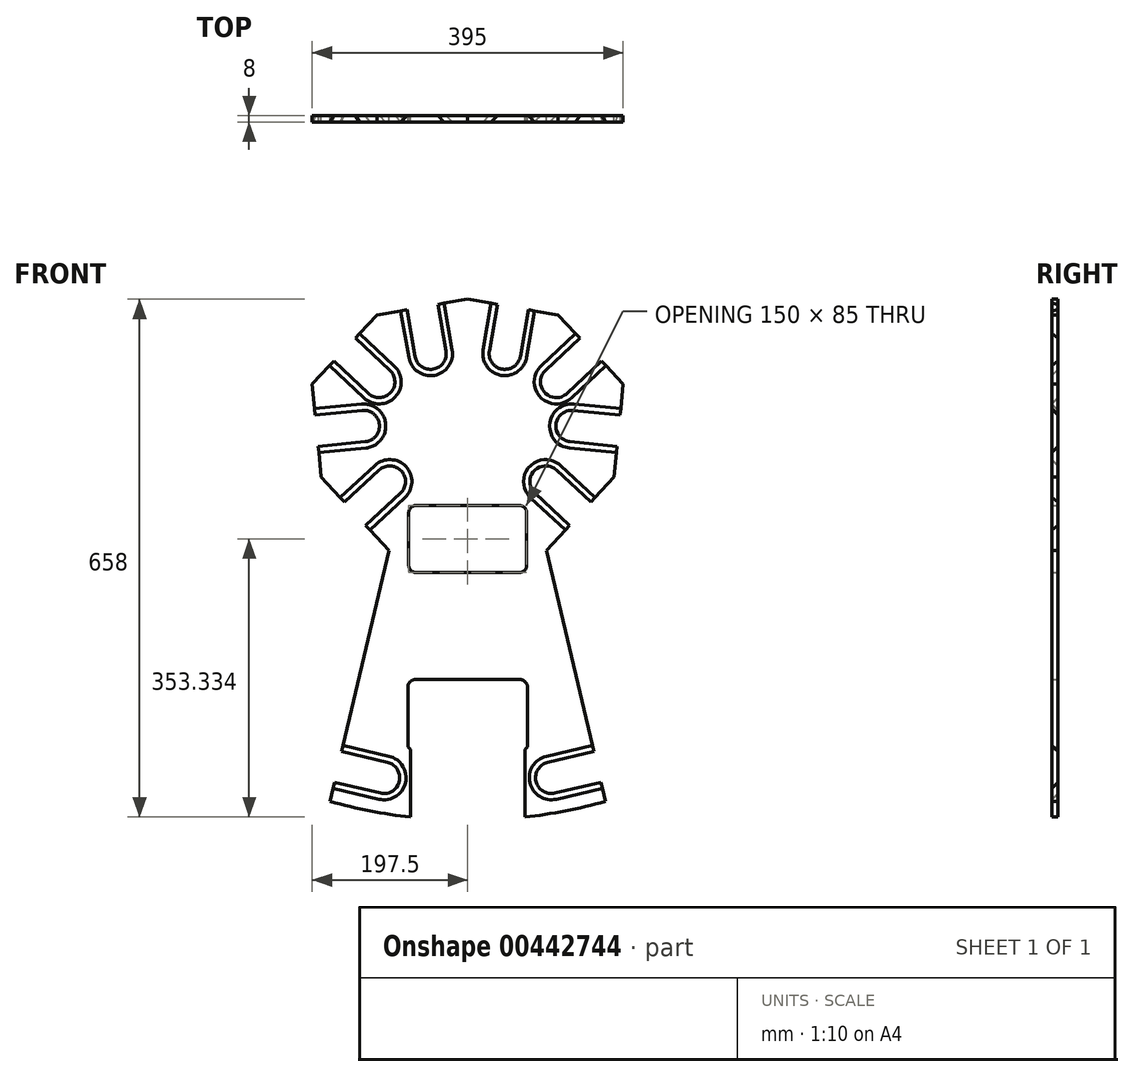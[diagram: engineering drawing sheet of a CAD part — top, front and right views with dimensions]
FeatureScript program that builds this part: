
annotation { "Feature Type Name" : "Feature", "Feature Type Description" : "" }
export const myFeature = defineFeature(function(context is Context, id is Id, definition is map)
    precondition{}
    {
        {
            var Q0;
            Q0=qCreatedBy(makeId("Front.planeOp"),FACE);
            var sketch = newSketch(context, id + "F0", { "sketchPlane" : qUnion([Q0])});
            skLineSegment(sketch, "E0", {"start": v(0, -18.17) * mm, "end": v(65.8, -18.17) * mm});
            skArc(sketch, "E1", {"start": v(65.8, -18.17) * mm, "mid": v(72.3, -15.47) * mm, "end": v(75, -8.97) * mm});
            skLineSegment(sketch, "E2", {"start": v(75, -8.97) * mm, "end": v(75, 57.63) * mm});
            skArc(sketch, "E3", {"start": v(75, 57.63) * mm, "mid": v(72.3, 64.14) * mm, "end": v(65.8, 66.83) * mm});
            skLineSegment(sketch, "E4", {"start": v(65.8, 66.83) * mm, "end": v(0, 66.83) * mm});
            skLineSegment(sketch, "E5", {"start": v(76, -239.94) * mm, "end": v(72.5, -242.91) * mm});
            skLineSegment(sketch, "E6", {"start": v(76, -239.94) * mm, "end": v(76, -164) * mm});
            skLineSegment(sketch, "E7", {"start": v(66, -154) * mm, "end": v(0, -154) * mm});
            skArc(sketch, "E8", {"start": v(76, -164) * mm, "mid": v(73.07, -156.93) * mm, "end": v(66, -154) * mm});
            skArc(sketch, "E9", {"start": v(101.72, -259.46) * mm, "mid": v(86.82, -283.5) * mm, "end": v(110.87, -298.4) * mm});
            skLineSegment(sketch, "E10", {"start": v(101.72, -259.46) * mm, "end": v(160.12, -245.73) * mm});
            skLineSegment(sketch, "E11", {"start": v(110.87, -298.4) * mm, "end": v(169.28, -284.66) * mm});
            skLineSegment(sketch, "E12", {"start": v(0, 329) * mm, "end": v(37.8, 322.43) * mm});
            skLineSegment(sketch, "E13", {"start": v(115, 309) * mm, "end": v(142.57, 279.6) * mm});
            skLineSegment(sketch, "E14", {"start": v(197.5, 221) * mm, "end": v(193.69, 181.9) * mm});
            skLineSegment(sketch, "E15", {"start": v(186, 103) * mm, "end": v(156.58, 71.18) * mm});
            skLineSegment(sketch, "E16", {"start": v(100, 10) * mm, "end": v(160.12, -245.73) * mm});
            skLineSegment(sketch, "E17", {"start": v(72.5, -329) * mm, "end": v(72.5, -242.91) * mm});
            skArc(sketch, "E18", {"start": v(72.5, -329) * mm, "mid": v(124.15, -321.07) * mm, "end": v(175, -309) * mm});
            skArc(sketch, "E19", {"start": v(112.53, 111.92) * mm, "mid": v(84.26, 110.81) * mm, "end": v(85.37, 82.55) * mm});
            skLineSegment(sketch, "E20", {"start": v(112.53, 111.92) * mm, "end": v(156.58, 71.18) * mm});
            skLineSegment(sketch, "E21", {"start": v(85.37, 82.55) * mm, "end": v(129.42, 41.82) * mm});
            skArc(sketch, "E22", {"start": v(133.97, 187.73) * mm, "mid": v(112.13, 169.76) * mm, "end": v(130.1, 147.91) * mm});
            skLineSegment(sketch, "E23", {"start": v(133.97, 187.73) * mm, "end": v(193.69, 181.9) * mm});
            skLineSegment(sketch, "E24", {"start": v(130.1, 147.91) * mm, "end": v(189.81, 142.1) * mm});
            skArc(sketch, "E25", {"start": v(98.8, 238.55) * mm, "mid": v(97.89, 210.28) * mm, "end": v(126.16, 209.37) * mm});
            skLineSegment(sketch, "E26", {"start": v(98.8, 238.55) * mm, "end": v(142.57, 279.6) * mm});
            skLineSegment(sketch, "E27", {"start": v(126.16, 209.37) * mm, "end": v(169.93, 250.4) * mm});
            skArc(sketch, "E28", {"start": v(27.52, 263.31) * mm, "mid": v(43.8, 240.18) * mm, "end": v(66.92, 256.46) * mm});
            skLineSegment(sketch, "E29", {"start": v(27.52, 263.31) * mm, "end": v(37.8, 322.43) * mm});
            skLineSegment(sketch, "E30", {"start": v(66.92, 256.46) * mm, "end": v(77.2, 315.57) * mm});
            skLineSegment(sketch, "E31", {"start": v(129.42, 41.82) * mm, "end": v(100, 10) * mm});
            skLineSegment(sketch, "E32", {"start": v(189.81, 142.1) * mm, "end": v(186, 103) * mm});
            skLineSegment(sketch, "E33", {"start": v(169.93, 250.4) * mm, "end": v(197.5, 221) * mm});
            skLineSegment(sketch, "E34", {"start": v(77.2, 315.57) * mm, "end": v(115, 309) * mm});
            skLineSegment(sketch, "E35", {"start": v(169.28, -284.66) * mm, "end": v(175, -309) * mm});
            skArc(sketch, "E36", {"start": v(-75, -8.97) * mm, "mid": v(-72.3, -15.47) * mm, "end": v(-65.8, -18.17) * mm});
            skLineSegment(sketch, "E37", {"start": v(-75, -8.97) * mm, "end": v(-75, 57.63) * mm});
            skArc(sketch, "E38", {"start": v(-65.8, 66.83) * mm, "mid": v(-72.3, 64.14) * mm, "end": v(-75, 57.63) * mm});
            skLineSegment(sketch, "E39", {"start": v(-76, -239.94) * mm, "end": v(-72.5, -242.91) * mm});
            skLineSegment(sketch, "E40", {"start": v(-76, -239.94) * mm, "end": v(-76, -164) * mm});
            skLineSegment(sketch, "E41", {"start": v(-66, -154) * mm, "end": v(0, -154) * mm});
            skArc(sketch, "E42", {"start": v(-66, -154) * mm, "mid": v(-73.07, -156.93) * mm, "end": v(-76, -164) * mm});
            skArc(sketch, "E43", {"start": v(-110.87, -298.4) * mm, "mid": v(-86.82, -283.5) * mm, "end": v(-101.72, -259.46) * mm});
            skLineSegment(sketch, "E44", {"start": v(-101.72, -259.46) * mm, "end": v(-160.12, -245.73) * mm});
            skLineSegment(sketch, "E45", {"start": v(-110.87, -298.4) * mm, "end": v(-169.28, -284.66) * mm});
            skLineSegment(sketch, "E46", {"start": v(-72.5, -329) * mm, "end": v(-72.5, -242.91) * mm});
            skArc(sketch, "E47", {"start": v(-175, -309) * mm, "mid": v(-124.15, -321.07) * mm, "end": v(-72.5, -329) * mm});
            skArc(sketch, "E48", {"start": v(-85.37, 82.55) * mm, "mid": v(-84.26, 110.81) * mm, "end": v(-112.53, 111.92) * mm});
            skLineSegment(sketch, "E49", {"start": v(-112.53, 111.92) * mm, "end": v(-156.58, 71.18) * mm});
            skLineSegment(sketch, "E50", {"start": v(-85.37, 82.55) * mm, "end": v(-129.42, 41.82) * mm});
            skArc(sketch, "E51", {"start": v(-130.1, 147.91) * mm, "mid": v(-112.13, 169.76) * mm, "end": v(-133.97, 187.73) * mm});
            skLineSegment(sketch, "E52", {"start": v(-133.97, 187.73) * mm, "end": v(-193.69, 181.9) * mm});
            skLineSegment(sketch, "E53", {"start": v(-130.1, 147.91) * mm, "end": v(-189.81, 142.1) * mm});
            skArc(sketch, "E54", {"start": v(-126.16, 209.37) * mm, "mid": v(-97.89, 210.28) * mm, "end": v(-98.8, 238.55) * mm});
            skLineSegment(sketch, "E55", {"start": v(-98.8, 238.55) * mm, "end": v(-142.57, 279.6) * mm});
            skLineSegment(sketch, "E56", {"start": v(-126.16, 209.37) * mm, "end": v(-169.93, 250.4) * mm});
            skArc(sketch, "E57", {"start": v(-66.92, 256.46) * mm, "mid": v(-43.8, 240.18) * mm, "end": v(-27.52, 263.31) * mm});
            skLineSegment(sketch, "E58", {"start": v(-27.52, 263.31) * mm, "end": v(-37.8, 322.43) * mm});
            skLineSegment(sketch, "E59", {"start": v(-66.92, 256.46) * mm, "end": v(-77.2, 315.57) * mm});
            skLineSegment(sketch, "E60", {"start": v(-129.42, 41.82) * mm, "end": v(-100, 10) * mm});
            skLineSegment(sketch, "E61", {"start": v(-186, 103) * mm, "end": v(-156.58, 71.18) * mm});
            skLineSegment(sketch, "E62", {"start": v(-189.81, 142.1) * mm, "end": v(-186, 103) * mm});
            skLineSegment(sketch, "E63", {"start": v(-197.5, 221) * mm, "end": v(-193.69, 181.9) * mm});
            skLineSegment(sketch, "E64", {"start": v(-169.93, 250.4) * mm, "end": v(-197.5, 221) * mm});
            skLineSegment(sketch, "E65", {"start": v(-115, 309) * mm, "end": v(-142.57, 279.6) * mm});
            skLineSegment(sketch, "E66", {"start": v(-77.2, 315.57) * mm, "end": v(-115, 309) * mm});
            skLineSegment(sketch, "E67", {"start": v(0, 329) * mm, "end": v(-37.8, 322.43) * mm});
            skLineSegment(sketch, "E68", {"start": v(-169.28, -284.66) * mm, "end": v(-175, -309) * mm});
            skLineSegment(sketch, "E69", {"start": v(-100, 10) * mm, "end": v(-160.12, -245.73) * mm});
            skLineSegment(sketch, "E70", {"start": v(-65.8, 66.83) * mm, "end": v(0, 66.83) * mm});
            skLineSegment(sketch, "E71", {"start": v(0, -18.17) * mm, "end": v(-65.8, -18.17) * mm});
            skSolve(sketch);
        }
        {
            var Q0;
            Q0 = qSketchRegion(id + "F0", true);
            extrude(context, id + "F1", {"entities" : qUnion([Q0]), "depth" : 8 * mm});
        }
        {
            var Q0;
            Q0=makeQuery(id+"F1.opExtrude","SWEPT_FACE",FACE,{"disambiguationData":[OSD([sQuery(id+"F0.wireOp",EDGE,"E35")])]});
            var sketch = newSketch(context, id + "F2", { "sketchPlane" : qUnion([Q0])});
            skLineSegment(sketch, "E72.0", {"start": v(-8, -315.85) * mm, "end": v(0, -315.85) * mm});
            skLineSegment(sketch, "E73", {"start": v(-8, -315.85) * mm, "end": v(-8, -323.85) * mm});
            skLineSegment(sketch, "E74", {"start": v(-8, -323.85) * mm, "end": v(0, -315.85) * mm});
            skSolve(sketch);
        }
        {
            var Q0;
            Q0 = qSketchRegion(id + "F2", true);
            var Q1;
            Q1=makeQuery(id+"F1.opExtrude","CAP_EDGE",EDGE,{"disambiguationData":[OSD([sQuery(id+"F0.wireOp",EDGE,"E11")])],"isStart":false});
            var Q2;
            Q2=makeQuery(id+"F1.opExtrude","CAP_EDGE",EDGE,{"disambiguationData":[OSD([sQuery(id+"F0.wireOp",EDGE,"E9")])],"isStart":false});
            var Q3;
            Q3=makeQuery(id+"F1.opExtrude","CAP_EDGE",EDGE,{"disambiguationData":[OSD([sQuery(id+"F0.wireOp",EDGE,"E10")])],"isStart":false});
            sweep(context, id + "F3", {"operationType" : NewBodyOperationType.REMOVE, "profiles" : qUnion([Q0]), "path" : qUnion([Q1, Q2, Q3])});
        }
        {
            var Q0;
            Q0=makeQuery(id+"F1.opExtrude","SWEPT_FACE",FACE,{"disambiguationData":[OSD([sQuery(id+"F0.wireOp",EDGE,"E31")])]});
            var sketch = newSketch(context, id + "F4", { "sketchPlane" : qUnion([Q0])});
            skLineSegment(sketch, "E75.0", {"start": v(-8, 118.57) * mm, "end": v(0, 118.57) * mm});
            skLineSegment(sketch, "E76", {"start": v(-8, 118.57) * mm, "end": v(-8, 110.57) * mm});
            skLineSegment(sketch, "E77", {"start": v(-8, 110.57) * mm, "end": v(0, 118.57) * mm});
            skSolve(sketch);
        }
        {
            var Q0;
            Q0 = qSketchRegion(id + "F4", true);
            var Q1;
            Q1=makeQuery(id+"F1.opExtrude","CAP_EDGE",EDGE,{"disambiguationData":[OSD([sQuery(id+"F0.wireOp",EDGE,"E21")])],"isStart":false});
            var Q2;
            Q2=makeQuery(id+"F1.opExtrude","CAP_EDGE",EDGE,{"disambiguationData":[OSD([sQuery(id+"F0.wireOp",EDGE,"E19")])],"isStart":false});
            var Q3;
            Q3=makeQuery(id+"F1.opExtrude","CAP_EDGE",EDGE,{"disambiguationData":[OSD([sQuery(id+"F0.wireOp",EDGE,"E20")])],"isStart":false});
            sweep(context, id + "F5", {"operationType" : NewBodyOperationType.REMOVE, "profiles" : qUnion([Q0]), "path" : qUnion([Q1, Q2, Q3])});
        }
        {
            var Q0;
            Q0=makeQuery(id+"F1.opExtrude","SWEPT_FACE",FACE,{"disambiguationData":[OSD([sQuery(id+"F0.wireOp",EDGE,"E32")])]});
            var sketch = newSketch(context, id + "F6", { "sketchPlane" : qUnion([Q0])});
            skLineSegment(sketch, "E78.0", {"start": v(-8, 159.84) * mm, "end": v(0, 159.84) * mm});
            skLineSegment(sketch, "E79", {"start": v(-8, 159.84) * mm, "end": v(-8, 151.84) * mm});
            skLineSegment(sketch, "E80", {"start": v(-8, 151.84) * mm, "end": v(0, 159.84) * mm});
            skSolve(sketch);
        }
        {
            var Q0;
            Q0 = qSketchRegion(id + "F6", true);
            var Q1;
            Q1=makeQuery(id+"F1.opExtrude","CAP_EDGE",EDGE,{"disambiguationData":[OSD([sQuery(id+"F0.wireOp",EDGE,"E24")])],"isStart":false});
            var Q2;
            Q2=makeQuery(id+"F1.opExtrude","CAP_EDGE",EDGE,{"disambiguationData":[OSD([sQuery(id+"F0.wireOp",EDGE,"E22")])],"isStart":false});
            var Q3;
            Q3=makeQuery(id+"F1.opExtrude","CAP_EDGE",EDGE,{"disambiguationData":[OSD([sQuery(id+"F0.wireOp",EDGE,"E23")])],"isStart":false});
            sweep(context, id + "F7", {"operationType" : NewBodyOperationType.REMOVE, "profiles" : qUnion([Q0]), "path" : qUnion([Q1, Q2, Q3])});
        }
        {
            var Q0;
            Q0=makeQuery(id+"F1.opExtrude","SWEPT_FACE",FACE,{"disambiguationData":[OSD([sQuery(id+"F0.wireOp",EDGE,"E33")])]});
            var sketch = newSketch(context, id + "F8", { "sketchPlane" : qUnion([Q0])});
            skLineSegment(sketch, "E81.0", {"start": v(-8, 66.46) * mm, "end": v(0, 66.46) * mm});
            skLineSegment(sketch, "E82", {"start": v(-8, 66.46) * mm, "end": v(-8, 58.46) * mm});
            skLineSegment(sketch, "E83", {"start": v(-8, 58.46) * mm, "end": v(0, 66.46) * mm});
            skSolve(sketch);
        }
        {
            var Q0;
            Q0 = qSketchRegion(id + "F8", true);
            var Q1;
            Q1=makeQuery(id+"F1.opExtrude","CAP_EDGE",EDGE,{"disambiguationData":[OSD([sQuery(id+"F0.wireOp",EDGE,"E27")])],"isStart":false});
            var Q2;
            Q2=makeQuery(id+"F1.opExtrude","CAP_EDGE",EDGE,{"disambiguationData":[OSD([sQuery(id+"F0.wireOp",EDGE,"E25")])],"isStart":false});
            var Q3;
            Q3=makeQuery(id+"F1.opExtrude","CAP_EDGE",EDGE,{"disambiguationData":[OSD([sQuery(id+"F0.wireOp",EDGE,"E26")])],"isStart":false});
            sweep(context, id + "F9", {"operationType" : NewBodyOperationType.REMOVE, "profiles" : qUnion([Q0]), "path" : qUnion([Q1, Q2, Q3])});
        }
        {
            var Q0;
            Q0=makeQuery(id+"F1.opExtrude","SWEPT_FACE",FACE,{"disambiguationData":[OSD([sQuery(id+"F0.wireOp",EDGE,"E34")])]});
            var sketch = newSketch(context, id + "F10", { "sketchPlane" : qUnion([Q0])});
            skLineSegment(sketch, "E84.0", {"start": v(22, -8) * mm, "end": v(22, 0) * mm});
            skLineSegment(sketch, "E85", {"start": v(22, -8) * mm, "end": v(30, -8) * mm});
            skLineSegment(sketch, "E86", {"start": v(30, -8) * mm, "end": v(22, 0) * mm});
            skSolve(sketch);
        }
        {
            var Q0;
            Q0 = qSketchRegion(id + "F10", true);
            var Q1;
            Q1=makeQuery(id+"F1.opExtrude","CAP_EDGE",EDGE,{"disambiguationData":[OSD([sQuery(id+"F0.wireOp",EDGE,"E30")])],"isStart":false});
            var Q2;
            Q2=makeQuery(id+"F1.opExtrude","CAP_EDGE",EDGE,{"disambiguationData":[OSD([sQuery(id+"F0.wireOp",EDGE,"E28")])],"isStart":false});
            var Q3;
            Q3=makeQuery(id+"F1.opExtrude","CAP_EDGE",EDGE,{"disambiguationData":[OSD([sQuery(id+"F0.wireOp",EDGE,"E29")])],"isStart":false});
            sweep(context, id + "F11", {"operationType" : NewBodyOperationType.REMOVE, "profiles" : qUnion([Q0]), "path" : qUnion([Q1, Q2, Q3])});
        }
        {
            var Q0;
            Q0=makeQuery(id+"F1.opExtrude","SWEPT_FACE",FACE,{"disambiguationData":[OSD([sQuery(id+"F0.wireOp",EDGE,"E67")])]});
            var sketch = newSketch(context, id + "F12", { "sketchPlane" : qUnion([Q0])});
            skLineSegment(sketch, "E87.0", {"start": v(18, -8) * mm, "end": v(18, 0) * mm});
            skLineSegment(sketch, "E88", {"start": v(18, -8) * mm, "end": v(26, -8) * mm});
            skLineSegment(sketch, "E89", {"start": v(26, -8) * mm, "end": v(18, 0) * mm});
            skSolve(sketch);
        }
        {
            var Q0;
            Q0 = qSketchRegion(id + "F12", true);
            var Q1;
            Q1=makeQuery(id+"F1.opExtrude","CAP_EDGE",EDGE,{"disambiguationData":[OSD([sQuery(id+"F0.wireOp",EDGE,"E58")])],"isStart":false});
            var Q2;
            Q2=makeQuery(id+"F1.opExtrude","CAP_EDGE",EDGE,{"disambiguationData":[OSD([sQuery(id+"F0.wireOp",EDGE,"E57")])],"isStart":false});
            var Q3;
            Q3=makeQuery(id+"F1.opExtrude","CAP_EDGE",EDGE,{"disambiguationData":[OSD([sQuery(id+"F0.wireOp",EDGE,"E59")])],"isStart":false});
            sweep(context, id + "F13", {"operationType" : NewBodyOperationType.REMOVE, "profiles" : qUnion([Q0]), "path" : qUnion([Q1, Q2, Q3])});
        }
        {
            var Q0;
            Q0=makeQuery(id+"F1.opExtrude","SWEPT_FACE",FACE,{"disambiguationData":[OSD([sQuery(id+"F0.wireOp",EDGE,"E65")])]});
            var sketch = newSketch(context, id + "F14", { "sketchPlane" : qUnion([Q0])});
            skLineSegment(sketch, "E90.0", {"start": v(8, 106.46) * mm, "end": v(0, 106.46) * mm});
            skLineSegment(sketch, "E91", {"start": v(8, 106.46) * mm, "end": v(8, 114.46) * mm});
            skLineSegment(sketch, "E92", {"start": v(8, 114.46) * mm, "end": v(0, 106.46) * mm});
            skSolve(sketch);
        }
        {
            var Q0;
            Q0 = qSketchRegion(id + "F14", true);
            var Q1;
            Q1=makeQuery(id+"F1.opExtrude","CAP_EDGE",EDGE,{"disambiguationData":[OSD([sQuery(id+"F0.wireOp",EDGE,"E54")])],"isStart":false});
            var Q2;
            Q2=makeQuery(id+"F1.opExtrude","CAP_EDGE",EDGE,{"disambiguationData":[OSD([sQuery(id+"F0.wireOp",EDGE,"E55")])],"isStart":false});
            var Q3;
            Q3=makeQuery(id+"F1.opExtrude","CAP_EDGE",EDGE,{"disambiguationData":[OSD([sQuery(id+"F0.wireOp",EDGE,"E56")])],"isStart":false});
            sweep(context, id + "F15", {"operationType" : NewBodyOperationType.REMOVE, "profiles" : qUnion([Q0]), "path" : qUnion([Q1, Q2, Q3])});
        }
        {
            var Q0;
            Q0=makeQuery(id+"F1.opExtrude","SWEPT_FACE",FACE,{"disambiguationData":[OSD([sQuery(id+"F0.wireOp",EDGE,"E63")])]});
            var sketch = newSketch(context, id + "F16", { "sketchPlane" : qUnion([Q0])});
            skLineSegment(sketch, "E93.0", {"start": v(8, 199.84) * mm, "end": v(0, 199.84) * mm});
            skLineSegment(sketch, "E94", {"start": v(8, 199.84) * mm, "end": v(8, 207.84) * mm});
            skLineSegment(sketch, "E95", {"start": v(8, 207.84) * mm, "end": v(0, 199.84) * mm});
            skSolve(sketch);
        }
        {
            var Q0;
            Q0 = qSketchRegion(id + "F16", true);
            var Q1;
            Q1=makeQuery(id+"F1.opExtrude","CAP_EDGE",EDGE,{"disambiguationData":[OSD([sQuery(id+"F0.wireOp",EDGE,"E52")])],"isStart":false});
            var Q2;
            Q2=makeQuery(id+"F1.opExtrude","CAP_EDGE",EDGE,{"disambiguationData":[OSD([sQuery(id+"F0.wireOp",EDGE,"E51")])],"isStart":false});
            var Q3;
            Q3=makeQuery(id+"F1.opExtrude","CAP_EDGE",EDGE,{"disambiguationData":[OSD([sQuery(id+"F0.wireOp",EDGE,"E53")])],"isStart":false});
            sweep(context, id + "F17", {"operationType" : NewBodyOperationType.REMOVE, "profiles" : qUnion([Q0]), "path" : qUnion([Q1, Q2, Q3])});
        }
        {
            var Q0;
            Q0=makeQuery(id+"F1.opExtrude","SWEPT_FACE",FACE,{"disambiguationData":[OSD([sQuery(id+"F0.wireOp",EDGE,"E61")])]});
            var sketch = newSketch(context, id + "F18", { "sketchPlane" : qUnion([Q0])});
            skLineSegment(sketch, "E96.0", {"start": v(8, 158.57) * mm, "end": v(0, 158.57) * mm});
            skLineSegment(sketch, "E97", {"start": v(8, 158.57) * mm, "end": v(8, 166.57) * mm});
            skLineSegment(sketch, "E98", {"start": v(8, 166.57) * mm, "end": v(0, 158.57) * mm});
            skSolve(sketch);
        }
        {
            var Q0;
            Q0 = qSketchRegion(id + "F18", true);
            var Q1;
            Q1=makeQuery(id+"F1.opExtrude","CAP_EDGE",EDGE,{"disambiguationData":[OSD([sQuery(id+"F0.wireOp",EDGE,"E49")])],"isStart":false});
            var Q2;
            Q2=makeQuery(id+"F1.opExtrude","CAP_EDGE",EDGE,{"disambiguationData":[OSD([sQuery(id+"F0.wireOp",EDGE,"E48")])],"isStart":false});
            var Q3;
            Q3=makeQuery(id+"F1.opExtrude","CAP_EDGE",EDGE,{"disambiguationData":[OSD([sQuery(id+"F0.wireOp",EDGE,"E50")])],"isStart":false});
            sweep(context, id + "F19", {"operationType" : NewBodyOperationType.REMOVE, "profiles" : qUnion([Q0]), "path" : qUnion([Q1, Q2, Q3])});
        }
        {
            var Q0;
            Q0=makeQuery(id+"F1.opExtrude","SWEPT_FACE",FACE,{"disambiguationData":[OSD([sQuery(id+"F0.wireOp",EDGE,"E69")])]});
            var sketch = newSketch(context, id + "F20", { "sketchPlane" : qUnion([Q0])});
            skLineSegment(sketch, "E99.0", {"start": v(8, -275.85) * mm, "end": v(0, -275.85) * mm});
            skLineSegment(sketch, "E100", {"start": v(8, -275.85) * mm, "end": v(8, -267.85) * mm});
            skLineSegment(sketch, "E101", {"start": v(8, -267.85) * mm, "end": v(0, -275.85) * mm});
            skSolve(sketch);
        }
        {
            var Q0;
            Q0 = qSketchRegion(id + "F20", true);
            var Q1;
            Q1=makeQuery(id+"F1.opExtrude","CAP_EDGE",EDGE,{"disambiguationData":[OSD([sQuery(id+"F0.wireOp",EDGE,"E44")])],"isStart":false});
            var Q2;
            Q2=makeQuery(id+"F1.opExtrude","CAP_EDGE",EDGE,{"disambiguationData":[OSD([sQuery(id+"F0.wireOp",EDGE,"E43")])],"isStart":false});
            var Q3;
            Q3=makeQuery(id+"F1.opExtrude","CAP_EDGE",EDGE,{"disambiguationData":[OSD([sQuery(id+"F0.wireOp",EDGE,"E45")])],"isStart":false});
            sweep(context, id + "F21", {"operationType" : NewBodyOperationType.REMOVE, "profiles" : qUnion([Q0]), "path" : qUnion([Q1, Q2, Q3])});
        }
    });
